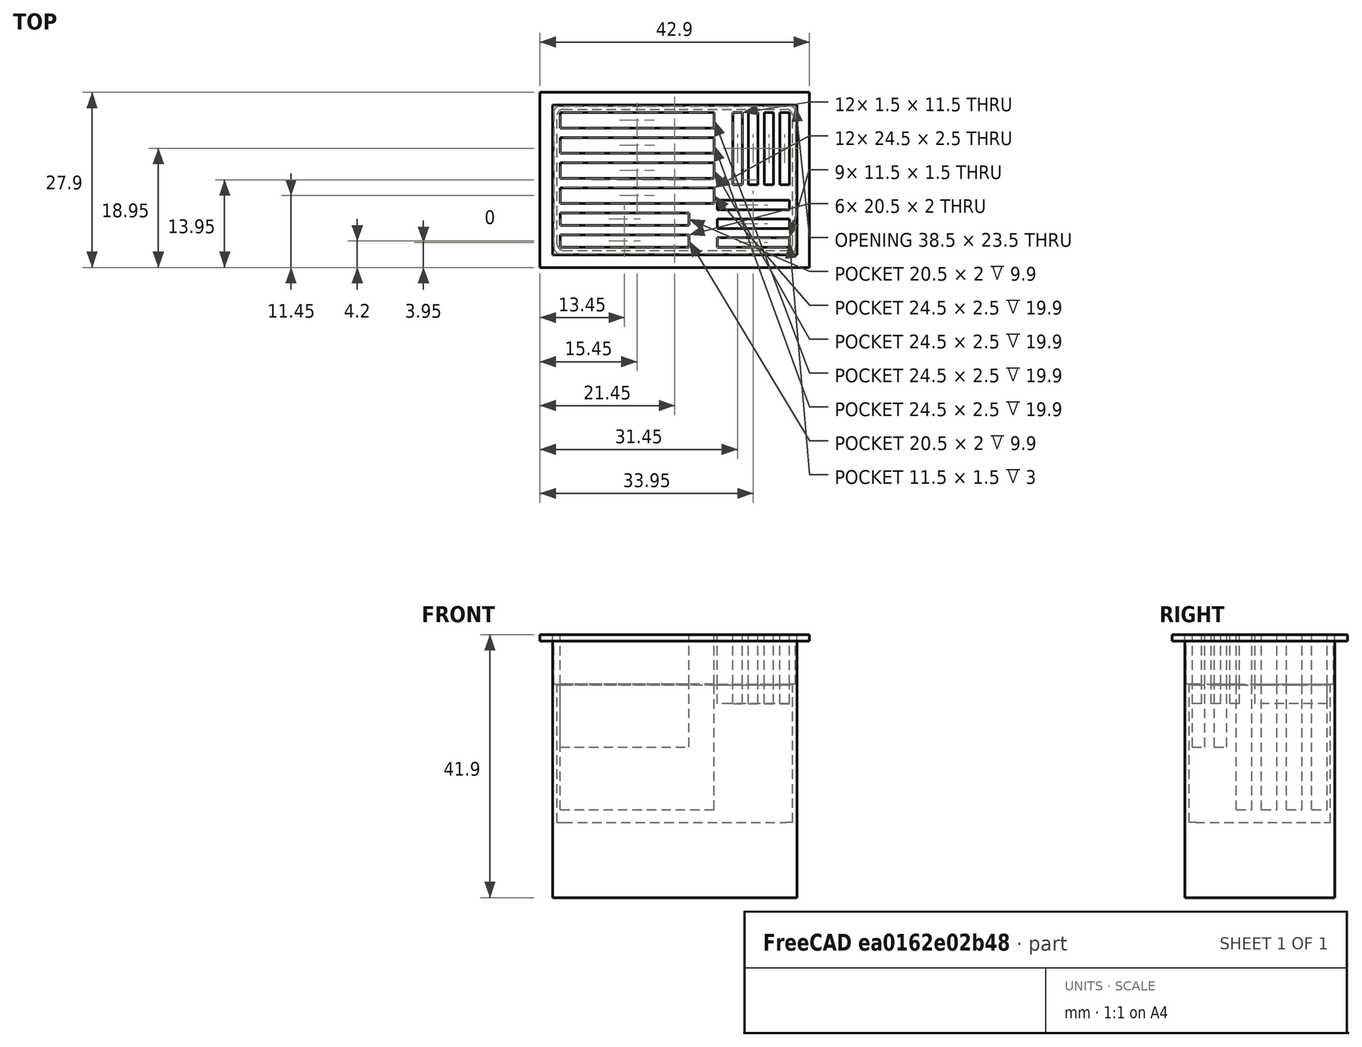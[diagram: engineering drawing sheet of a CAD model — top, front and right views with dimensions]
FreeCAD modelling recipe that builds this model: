
FCSTD DOCUMENT  (FreeCAD 0.18R14555 (Git shallow))
Label: sdcard-holder
License: All rights reserved
LicenseURL: http://en.wikipedia.org/wiki/All_rights_reserved
objects: Part::Box×17, Part::MultiFuse×2, Part::Fillet×2, Part::Cut×1, Part::Feature×1
note: 23 computed .brp shape members not serialized (recipe doc carries the construction recipe); baked Part::Feature solids carry a one-line shape summary decoded from their .brp

FEATURE [Part::Box] Box  label="Cube"
  AttacherType = Attacher::AttachEngine3D
  Height = 7.9
  Length = 38.5
  Placement = pos=(0.2,0.2,34) rot=(0,0,1;0rad)
  Width = 23.5
FEATURE [Part::Box] Box001  label="Cube001"
  AttacherType = Attacher::AttachEngine3D
  Height = 1
  Length = 42.9
  Placement = pos=(-2,-2,40.9) rot=(0,0,1;0rad)
  Width = 27.9
FEATURE [Part::Box] Box002  label="sd"
  AttacherType = Attacher::AttachEngine3D
  Height = 32
  Length = 24.5
  Placement = pos=(1.2,20.2,10) rot=(0,0,1;0rad)
  Width = 2.5
FEATURE [Part::Box] Box003  label="mini-sd"
  AttacherType = Attacher::AttachEngine3D
  Height = 22
  Length = 20.5
  Placement = pos=(1.2,1.2,20) rot=(0,0,1;0rad)
  Width = 2
FEATURE [Part::Box] Box004  label="micro-sd"
  AttacherType = Attacher::AttachEngine3D
  Height = 15
  Length = 11.5
  Placement = pos=(36.2,22.7,26.9) rot=(0,0,-1;1.5708rad)
  Width = 1.5
FEATURE [Part::Box] Box018  label="Cube002"
  AttacherType = Attacher::AttachEngine3D
  Height = 41.9
  Length = 38.9
  Width = 23.9
FEATURE [Part::Box] Box019  label="sd001"
  AttacherType = Attacher::AttachEngine3D
  Height = 32
  Length = 24.5
  Placement = pos=(1.2,16.2,10) rot=(0,0,1;0rad)
  Width = 2.5
FEATURE [Part::Box] Box020  label="sd002"
  AttacherType = Attacher::AttachEngine3D
  Height = 32
  Length = 24.5
  Placement = pos=(1.2,12.2,10) rot=(0,0,1;0rad)
  Width = 2.5
FEATURE [Part::Box] Box021  label="sd003"
  AttacherType = Attacher::AttachEngine3D
  Height = 32
  Length = 24.5
  Placement = pos=(1.2,8.2,10) rot=(0,0,1;0rad)
  Width = 2.5
FEATURE [Part::Box] Box022  label="mini-sd001"
  AttacherType = Attacher::AttachEngine3D
  Height = 22
  Length = 20.5
  Placement = pos=(1.2,4.7,20) rot=(0,0,1;0rad)
  Width = 2
FEATURE [Part::Box] Box023  label="micro-sd001"
  AttacherType = Attacher::AttachEngine3D
  Height = 15
  Length = 11.5
  Placement = pos=(33.7,22.7,26.9) rot=(0,0,-1;1.5708rad)
  Width = 1.5
FEATURE [Part::Box] Box024  label="micro-sd002"
  AttacherType = Attacher::AttachEngine3D
  Height = 15
  Length = 11.5
  Placement = pos=(31.2,22.7,26.9) rot=(0,0,-1;1.5708rad)
  Width = 1.5
FEATURE [Part::Box] Box025  label="micro-sd003"
  AttacherType = Attacher::AttachEngine3D
  Height = 15
  Length = 11.5
  Placement = pos=(37.7,2.7,26.9) rot=(0,0,1;3.14159rad)
  Width = 1.5
FEATURE [Part::Box] Box026  label="micro-sd004"
  AttacherType = Attacher::AttachEngine3D
  Height = 15
  Length = 11.5
  Placement = pos=(37.7,5.7,26.9) rot=(0,0,1;3.14159rad)
  Width = 1.5
FEATURE [Part::Box] Box027  label="micro-sd005"
  AttacherType = Attacher::AttachEngine3D
  Height = 15
  Length = 11.5
  Placement = pos=(37.7,8.7,26.9) rot=(0,0,1;3.14159rad)
  Width = 1.5
FEATURE [Part::Box] Box028  label="micro-sd006"
  AttacherType = Attacher::AttachEngine3D
  Height = 15
  Length = 11.5
  Placement = pos=(28.7,22.7,26.9) rot=(0,0,-1;1.5708rad)
  Width = 1.5
FEATURE [Part::MultiFuse] Fusion
  Placement = pos=(0,0,4) rot=(0,0,1;0rad)
  Shapes = -> [Box004,Box003,Box002,Box019,Box020,Box021,Box022,Box023,Box024,Box025,Box026,Box027,Box028]
FEATURE [Part::Box] Box029  label="Cube003"
  AttacherType = Attacher::AttachEngine3D
  Height = 21.9
  Length = 37.5
  Placement = pos=(0.7,0.7,12) rot=(0,0,1;0rad)
  Width = 22.5
FEATURE [Part::Fillet] Fillet
  Base = -> Box
  Edges = 4 edges r=1: [Edge1,Edge3,Edge5,Edge7]
FEATURE [Part::Fillet] Fillet001
  Base = -> Box029
  Edges = 4 edges r=1: [Edge1,Edge3,Edge5,Edge7]
FEATURE [Part::MultiFuse] Fusion001
  Shapes = -> [Fillet001,Fillet,Box001]
FEATURE [Part::Cut] Cut
  Base = -> Fusion001
  Tool = -> Fusion
FEATURE [Part::Feature] Cut001
  shape: bbox 42.9 x 27.9 x 29.9 mm, 142 faces, 2 solids (baked)
